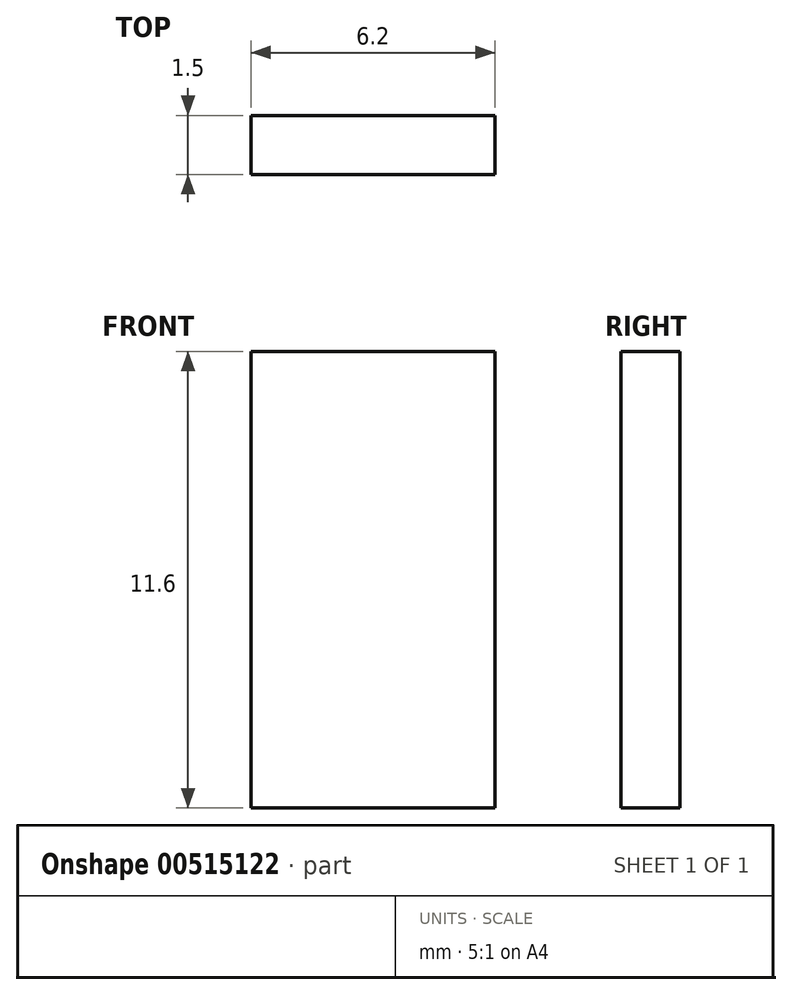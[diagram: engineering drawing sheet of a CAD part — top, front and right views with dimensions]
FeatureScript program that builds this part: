
annotation { "Feature Type Name" : "Feature", "Feature Type Description" : "" }
export const myFeature = defineFeature(function(context is Context, id is Id, definition is map)
    precondition{}
    {
        {
            var Q0;
            Q0=qCreatedBy(makeId("Front.planeOp"),FACE);
            var sketch = newSketch(context, id + "F0", { "sketchPlane" : qUnion([Q0])});
            skLineSegment(sketch, "E0.bottom", {"start": v(-3.1, 5.8) * mm, "end": v(3.1, 5.8) * mm});
            skLineSegment(sketch, "E0.top", {"start": v(-3.1, -5.8) * mm, "end": v(3.1, -5.8) * mm});
            skLineSegment(sketch, "E0.left", {"start": v(-3.1, 5.8) * mm, "end": v(-3.1, -5.8) * mm});
            skLineSegment(sketch, "E0.right", {"start": v(3.1, 5.8) * mm, "end": v(3.1, -5.8) * mm});
            skPoint(sketch, "E0.middle", {"position": v(0, 0) * mm});
            skSolve(sketch);
        }
        {
            var Q0;
            Q0=makeQuery(id+"F0.imprint","IMPRINT",FACE,{"disambiguationData":[TD([[makeQuery(id+"F0.imprint","IMPRINT",EDGE,{"derivedFrom":sQuery(id+"F0.wireOp",EDGE,"E0.bottom")}),-1.0]])]});
            extrude(context, id + "F1", {"entities" : qUnion([Q0]), "depth" : 1.5 * mm, "offsetDistance" : 25 * mm});
        }
    });
